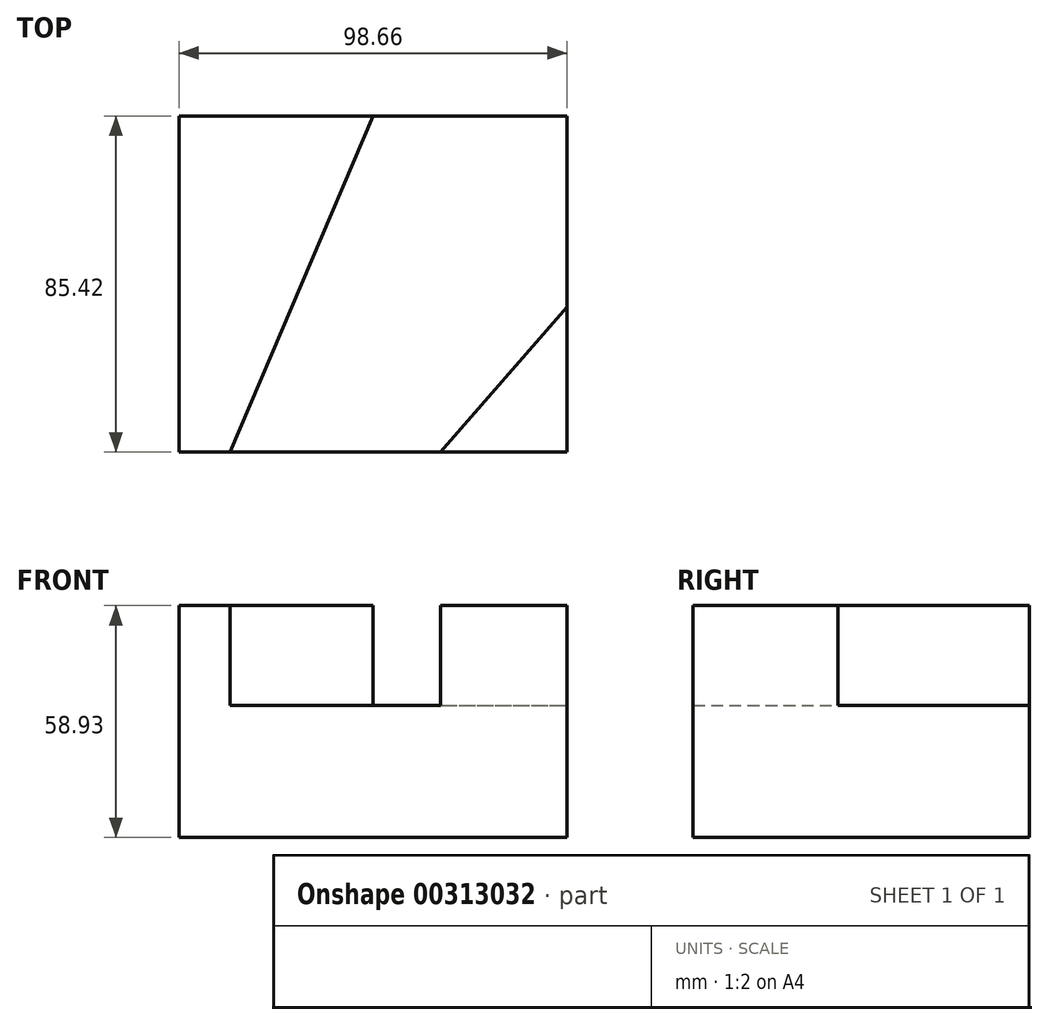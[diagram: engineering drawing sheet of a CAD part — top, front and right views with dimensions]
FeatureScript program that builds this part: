
annotation { "Feature Type Name" : "Feature", "Feature Type Description" : "" }
export const myFeature = defineFeature(function(context is Context, id is Id, definition is map)
    precondition{}
    {
        {
            var Q0;
            Q0=qCreatedBy(makeId("Top.planeOp"),FACE);
            var sketch = newSketch(context, id + "F0", { "sketchPlane" : qUnion([Q0])});
            skLineSegment(sketch, "E0.bottom", {"start": v(-50.13, 30.48) * mm, "end": v(48.53, 30.48) * mm});
            skLineSegment(sketch, "E0.top", {"start": v(-50.13, -54.94) * mm, "end": v(48.53, -54.94) * mm});
            skLineSegment(sketch, "E0.left", {"start": v(-50.13, 30.48) * mm, "end": v(-50.13, -54.94) * mm});
            skLineSegment(sketch, "E0.right", {"start": v(48.53, 30.48) * mm, "end": v(48.53, -54.94) * mm});
            skSolve(sketch);
        }
        {
            var Q0;
            Q0=makeQuery(id+"F0.imprint","IMPRINT",FACE,{"disambiguationData":[TD([[makeQuery(id+"F0.imprint","IMPRINT",EDGE,{"derivedFrom":sQuery(id+"F0.wireOp",EDGE,"E0.bottom")}),-1.0]])]});
            extrude(context, id + "F1", {"entities" : qUnion([Q0]), "depth" : 33.53 * mm});
        }
        {
            var Q0;
            Q0=makeQuery(id+"F1.opExtrude","CAP_FACE",FACE,{"disambiguationData":[OSD([sQuery(id+"F0.wireOp",EDGE,"E0.bottom"),sQuery(id+"F0.wireOp",EDGE,"E0.top"),sQuery(id+"F0.wireOp",EDGE,"E0.left"),sQuery(id+"F0.wireOp",EDGE,"E0.right")])],"isStart":false});
            var sketch = newSketch(context, id + "F2", { "sketchPlane" : qUnion([Q0])});
            skLineSegment(sketch, "E1", {"start": v(16.4, -54.94) * mm, "end": v(48.53, -18.12) * mm});
            skLineSegment(sketch, "E2", {"start": v(-37.14, -54.94) * mm, "end": v(-0.8, 30.48) * mm});
            skSolve(sketch);
        }
        {
            var Q0;
            {var subQ0=sQuery(id+"F2.wireOp",EDGE,"E2");Q0=makeQuery(id+"F2.imprint","IMPRINT",FACE,{"disambiguationData":[TD([[makeQuery(id+"F2.imprint","IMPRINT",EDGE,{"derivedFrom":subQ0}),1.0]])]});}
            var Q1;
            {var subQ0=sQuery(id+"F2.wireOp",EDGE,"E1");Q1=makeQuery(id+"F2.imprint","IMPRINT",FACE,{"disambiguationData":[TD([[makeQuery(id+"F2.imprint","IMPRINT",EDGE,{"derivedFrom":subQ0}),-1.0]])]});}
            extrude(context, id + "F3", {"entities" : qUnion([Q0, Q1]), "operationType" : NewBodyOperationType.ADD, "depth" : 25.4 * mm});
        }
    });
